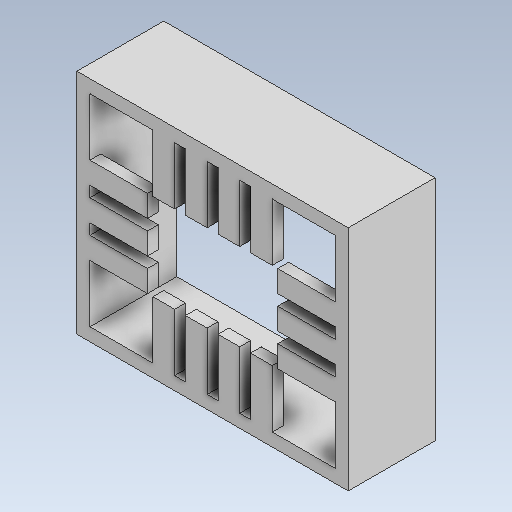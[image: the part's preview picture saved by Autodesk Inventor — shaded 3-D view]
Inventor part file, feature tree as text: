
AUTODESK INVENTOR PART (.ipt)
format: ipt  version: 2025.2 (Build 292293000, 293)  size: 450,048 bytes
history: native  units: mm
features: extrude x2, sketch x2
ambient origin geometry x8: Origin, YZ Plane, XZ Plane, XY Plane, X Axis, Y Axis, Z Axis, Center Point
bodies: Volumenkörper1 (feature_tree)
feature tree (4):
  extrude  "Extrusion1"  Depth=8.0mm
  extrude  "Extrusion2"  Depth=3.0mm
  sketch  "Skizze1"  dims[d2=12.0mm d3=8.0mm]
  sketch  "Skizze3"  dims[d9=24.6mm d10=3.0mm d12=3.0mm d14=28.6mm d15=3.0mm d16=3.0mm d17=5.3mm d18=5.3mm d20=5.3mm d21=2.0mm d22=2.0mm d23=2.0mm d24=1.0mm d25=1.0mm d26=2.0mm d27=2.0mm d28=2.0mm d29=2.0mm d30=1.0mm d31=1.0mm d32=1.0mm d33=0.5mm d34=0.5mm d35=1.0mm d36=0.0mm d37=1.5mm d38=1.5mm d39=1.5mm d40=1.5mm d41=7.0mm d42=0.0mm d43=21.0mm d44=25.0mm d50=3.0mm d51=1.8mm d52=1.8mm d54=1.8mm d55=0.5mm d56=0.872665mm d57=0.5mm d58=0.872665mm]
